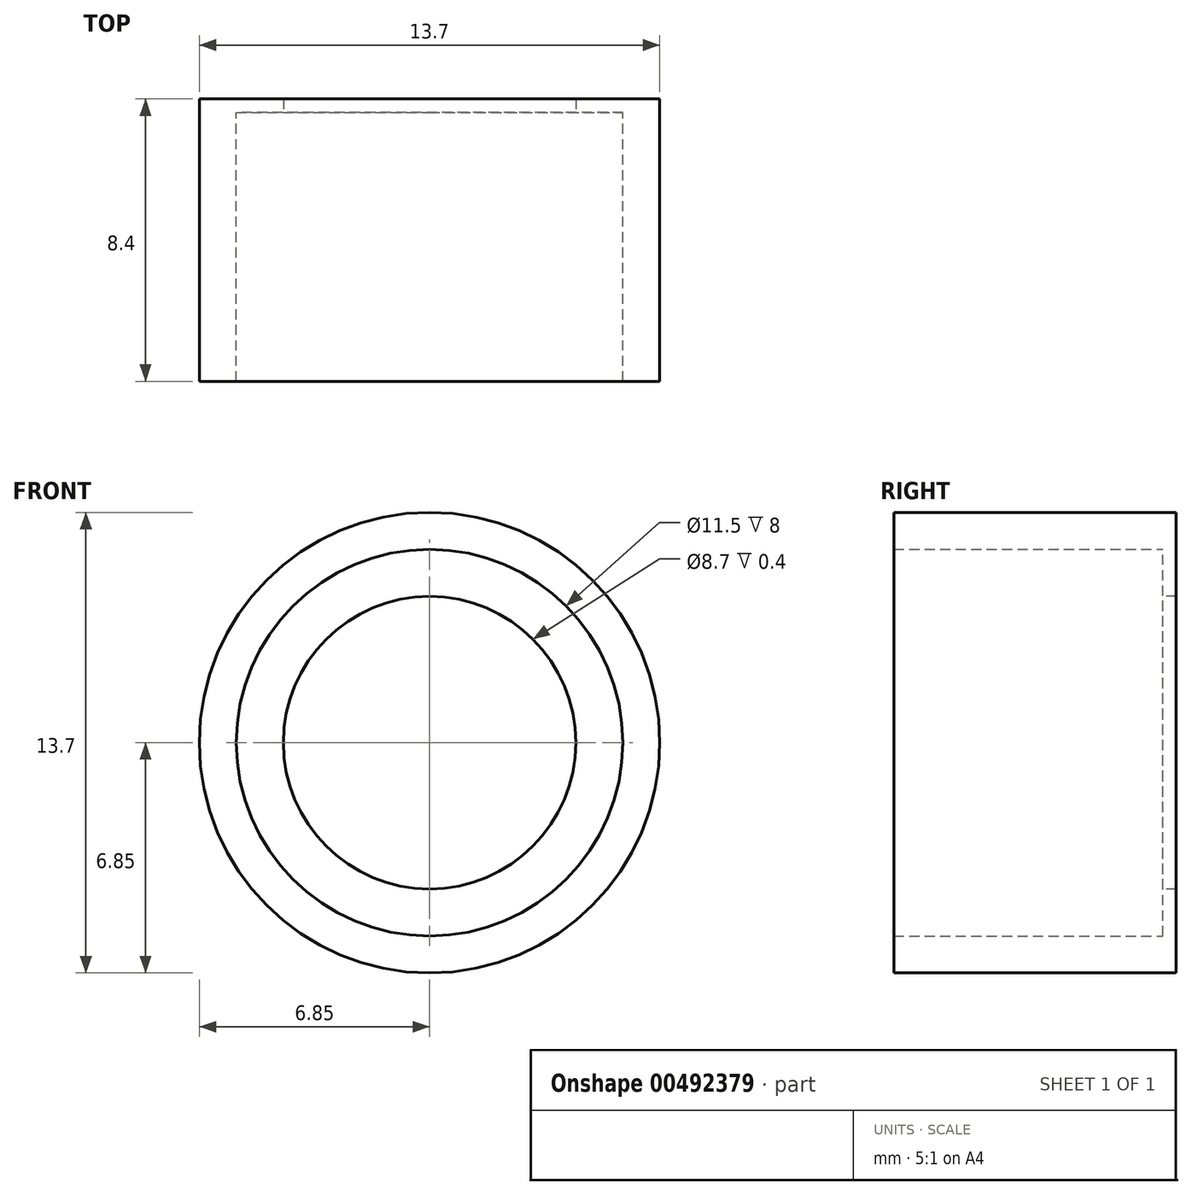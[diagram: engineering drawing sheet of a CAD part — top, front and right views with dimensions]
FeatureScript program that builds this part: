
annotation { "Feature Type Name" : "Feature", "Feature Type Description" : "" }
export const myFeature = defineFeature(function(context is Context, id is Id, definition is map)
    precondition{}
    {
        {
            var Q0;
            Q0=qCreatedBy(makeId("Front.planeOp"),FACE);
            var sketch = newSketch(context, id + "F0", { "sketchPlane" : qUnion([Q0])});
            skCircle(sketch, "E0", {"center": v(0, 0) * mm, "radius": 6.85 * mm});
            skCircle(sketch, "E1", {"center": v(0, 0) * mm, "radius": 5.75 * mm});
            skCircle(sketch, "E2", {"center": v(0, 0) * mm, "radius": 4.35 * mm});
            skSolve(sketch);
        }
        {
            var Q0;
            Q0=makeQuery(id+"F0.imprint","IMPRINT",FACE,{"disambiguationData":[TD([[makeQuery(id+"F0.imprint","IMPRINT",EDGE,{"derivedFrom":sQuery(id+"F0.wireOp",EDGE,"E0")}),1.0]])]});
            var Q1;
            Q1=makeQuery(id+"F0.imprint","IMPRINT",FACE,{"disambiguationData":[TD([[makeQuery(id+"F0.imprint","IMPRINT",EDGE,{"derivedFrom":sQuery(id+"F0.wireOp",EDGE,"E1")}),1.0]])]});
            var Q2;
            Q2=makeQuery(id+"F0.imprint","IMPRINT",FACE,{"disambiguationData":[TD([[makeQuery(id+"F0.imprint","IMPRINT",EDGE,{"derivedFrom":sQuery(id+"F0.wireOp",EDGE,"E2")}),1.0]])]});
            extrude(context, id + "F1", {"entities" : qUnion([Q0, Q1, Q2]), "depth" : 8 * mm});
        }
        {
            var Q0;
            Q0=makeQuery(id+"F0.imprint","IMPRINT",FACE,{"disambiguationData":[TD([[makeQuery(id+"F0.imprint","IMPRINT",EDGE,{"derivedFrom":sQuery(id+"F0.wireOp",EDGE,"E1")}),1.0]])]});
            var Q1;
            Q1=makeQuery(id+"F0.imprint","IMPRINT",FACE,{"disambiguationData":[TD([[makeQuery(id+"F0.imprint","IMPRINT",EDGE,{"derivedFrom":sQuery(id+"F0.wireOp",EDGE,"E2")}),1.0]])]});
            var Q2;
            Q2=sQuery(id+"F0.wireOp",EDGE,"E1");
            extrude(context, id + "F2", {"entities" : qUnion([Q0, Q1]), "operationType" : NewBodyOperationType.REMOVE, "surfaceEntities" : qUnion([Q2]), "depth" : 25 * mm});
        }
        {
            var Q0;
            Q0=makeQuery(id+"F0.imprint","IMPRINT",FACE,{"disambiguationData":[TD([[makeQuery(id+"F0.imprint","IMPRINT",EDGE,{"derivedFrom":sQuery(id+"F0.wireOp",EDGE,"E1")}),1.0]])]});
            var Q1;
            Q1=makeQuery(id+"F0.imprint","IMPRINT",FACE,{"disambiguationData":[TD([[makeQuery(id+"F0.imprint","IMPRINT",EDGE,{"derivedFrom":sQuery(id+"F0.wireOp",EDGE,"E0")}),1.0]])]});
            extrude(context, id + "F3", {"entities" : qUnion([Q0, Q1]), "operationType" : NewBodyOperationType.ADD, "oppositeDirection" : true, "depth" : .4 * mm});
        }
    });
